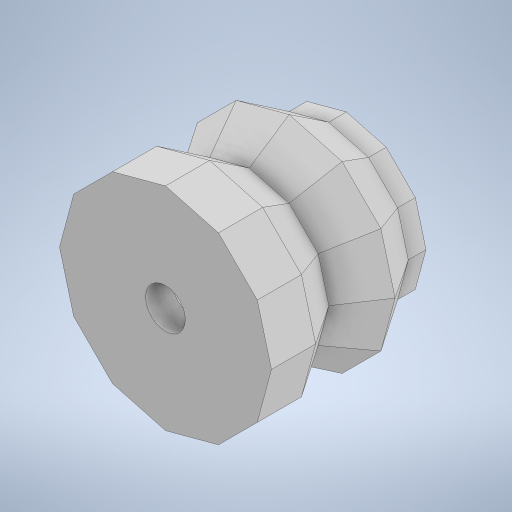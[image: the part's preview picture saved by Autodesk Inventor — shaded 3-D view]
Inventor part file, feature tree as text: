
AUTODESK INVENTOR PART (.ipt)
format: ipt  version: 2023 (Build 270158000, 158)  size: 358,912 bytes
history: native  units: in
note: dims shown in document units (in); Inventor stores cm internally (conversion verified against a paired STEP export)
features: sketch x6, extrude x4, projected_geometry x3, other x2, mirror x2, loft x1, shell x1
ambient origin geometry x8: Origin, YZ Plane, XZ Plane, XY Plane, X Axis, Y Axis, Z Axis, Center Point
bodies: Body1 (feature_tree)
feature tree (19):
  other  "솔리드1"
  sketch  "스케치1"
  other  "작업 평면1"
  loft  "로프트1"
  mirror  "미러1"
  mirror  "미러2"
  extrude  "돌출1"  Depth=0.1772in
  shell  "쉘1"  Thickness=0.7087in
  extrude  "돌출2"  TaperAngle=0.0deg  [1 undecoded]
  extrude  "돌출3"  TaperAngle=0.0deg  [1 undecoded]
  extrude  "돌출4"  Depth=0.0984in TaperAngle=0.0deg
  sketch  "스케치2"
  sketch  "스케치3"
  projected_geometry  "투영된 루프1"
  sketch  "스케치4"
  projected_geometry  "투영된 루프2"
  sketch  "스케치5"
  sketch  "스케치6"
  projected_geometry  "투영된 루프3"
note: 2 required parameter values undecoded (feature->parameter linkage not recoverable at this tier; creation-order binding heuristic only, values carry confidence <= 0.55)
